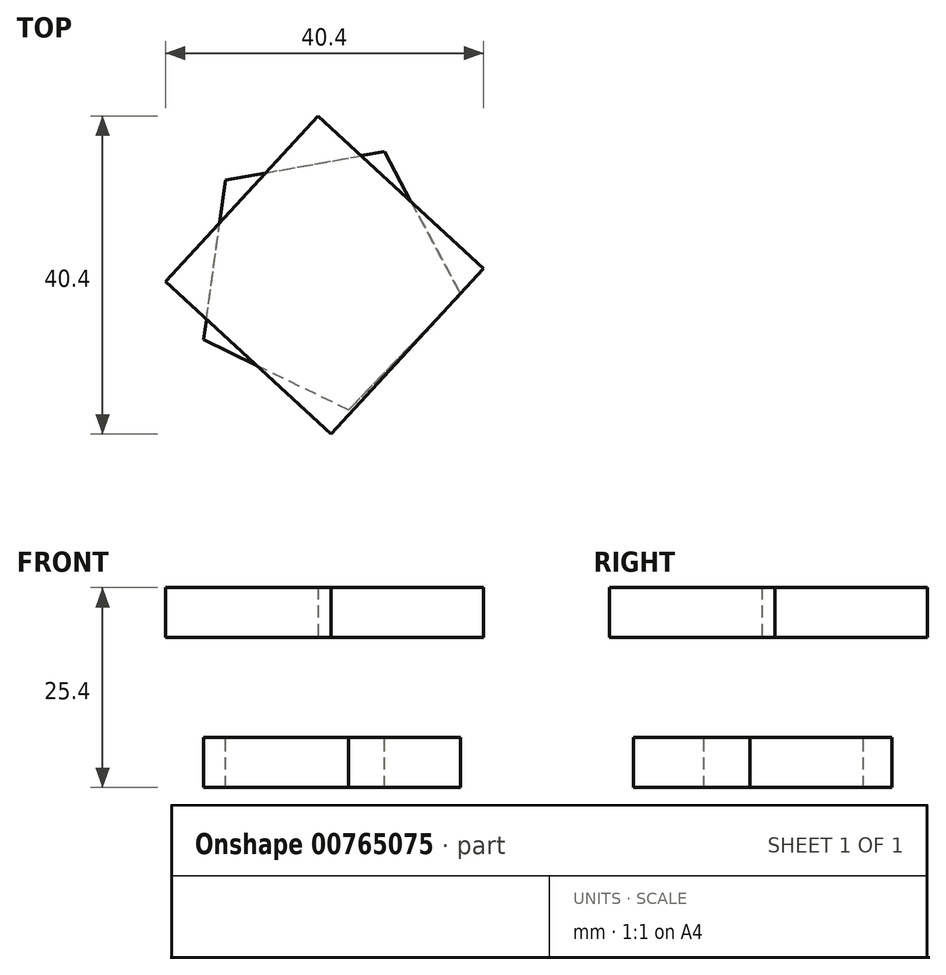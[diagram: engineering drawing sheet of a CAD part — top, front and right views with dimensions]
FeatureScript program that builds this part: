
annotation { "Feature Type Name" : "Feature", "Feature Type Description" : "" }
export const myFeature = defineFeature(function(context is Context, id is Id, definition is map)
    precondition{}
    {
        {
            var Q0;
            Q0=qCreatedBy(makeId("Top.planeOp"),FACE);
            cPlane(context, id + "F0", {"entities" : qUnion([Q0]), "cplaneType" : CPlaneType.OFFSET, "offset" : 12.7 * mm, "width" : 152.4 * mm, "height" : 152.4 * mm});
        }
        {
            var Q0;
            Q0=qCreatedBy(makeId("Top.planeOp"),FACE);
            var sketch = newSketch(context, id + "F1", { "sketchPlane" : qUnion([Q0])});
            skCircle(sketch, "E0.cCircle", {"center": v(0, 0) * mm, "radius": 14.1 * mm, "construction": true});
            skLineSegment(sketch, "E0.0", {"start": v(7.6, 15.68) * mm, "end": v(17.26, -2.38) * mm});
            skLineSegment(sketch, "E0.1", {"start": v(17.26, -2.38) * mm, "end": v(3.07, -17.15) * mm});
            skLineSegment(sketch, "E0.2", {"start": v(3.07, -17.15) * mm, "end": v(-15.36, -8.22) * mm});
            skLineSegment(sketch, "E0.3", {"start": v(-15.36, -8.22) * mm, "end": v(-12.56, 12.07) * mm});
            skLineSegment(sketch, "E0.4", {"start": v(-12.56, 12.07) * mm, "end": v(7.6, 15.68) * mm});
            skPoint(sketch, "E0.0.midPoint", {"position": v(12.43, 6.65) * mm});
            skSolve(sketch);
        }
        {
            var Q0;
            Q0=makeQuery(id+"F1.imprint","IMPRINT",FACE,{"disambiguationData":[TD([[makeQuery(id+"F1.imprint","IMPRINT",EDGE,{"derivedFrom":sQuery(id+"F1.wireOp",EDGE,"E0.0")}),-1.0]])]});
            extrude(context, id + "F2", {"entities" : qUnion([Q0]), "oppositeDirection" : true, "depth" : 6.35 * mm, "offsetDistance" : 25.4 * mm});
        }
        {
            var Q0;
            Q0=qCreatedBy(id+"F0.planeOp",FACE);
            var sketch = newSketch(context, id + "F3", { "sketchPlane" : qUnion([Q0])});
            skCircle(sketch, "E1.cCircle", {"center": v(0, 0) * mm, "radius": 14.3 * mm, "construction": true});
            skLineSegment(sketch, "E1.0", {"start": v(-0.84, 20.2) * mm, "end": v(20.2, 0.84) * mm});
            skLineSegment(sketch, "E1.1", {"start": v(20.2, 0.84) * mm, "end": v(0.84, -20.2) * mm});
            skLineSegment(sketch, "E1.2", {"start": v(0.84, -20.2) * mm, "end": v(-20.2, -0.84) * mm});
            skLineSegment(sketch, "E1.3", {"start": v(-20.2, -0.84) * mm, "end": v(-0.84, 20.2) * mm});
            skPoint(sketch, "E1.0.midPoint", {"position": v(9.68, 10.52) * mm});
            skSolve(sketch);
        }
        {
            var Q0;
            Q0=makeQuery(id+"F3.imprint","IMPRINT",FACE,{"disambiguationData":[TD([[makeQuery(id+"F3.imprint","IMPRINT",EDGE,{"derivedFrom":sQuery(id+"F3.wireOp",EDGE,"E1.0")}),-1.0]])]});
            extrude(context, id + "F4", {"entities" : qUnion([Q0]), "depth" : 6.35 * mm, "offsetDistance" : 25.4 * mm});
        }
    });
